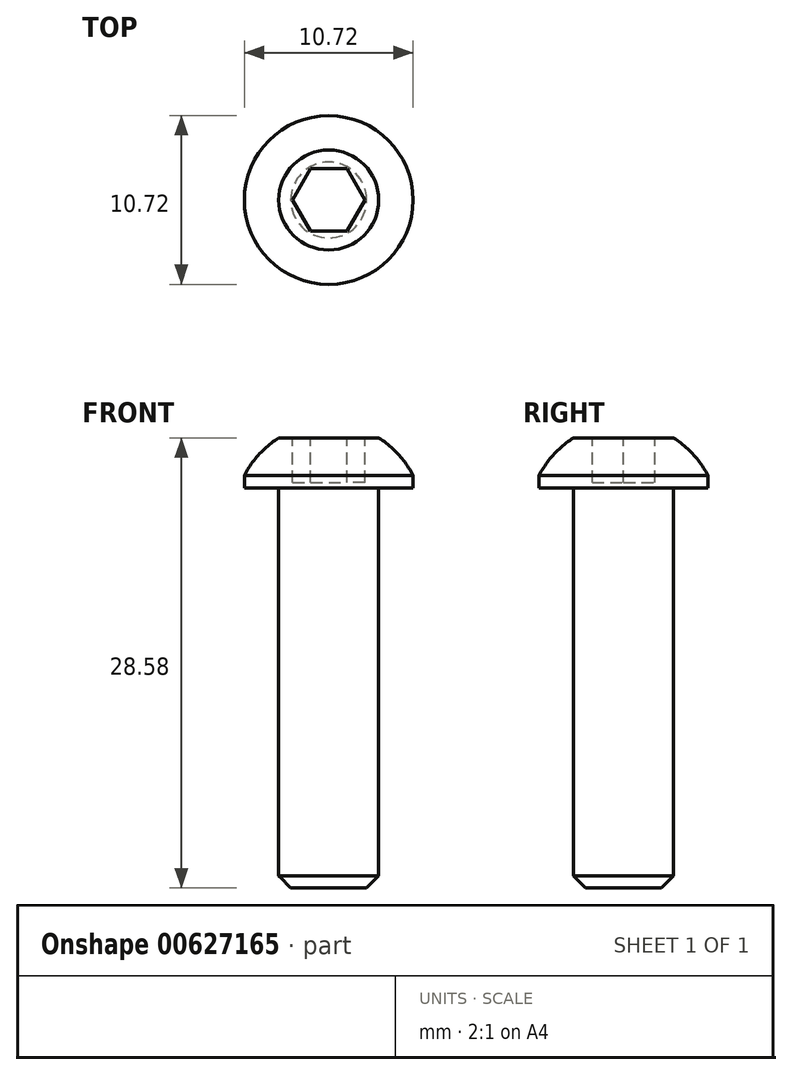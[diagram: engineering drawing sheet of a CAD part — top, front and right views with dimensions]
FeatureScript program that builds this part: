
annotation { "Feature Type Name" : "Feature", "Feature Type Description" : "" }
export const myFeature = defineFeature(function(context is Context, id is Id, definition is map)
    precondition{}
    {
        {
            var Q0;
            Q0=qCreatedBy(makeId("Front.planeOp"),FACE);
            var sketch = newSketch(context, id + "F0", { "sketchPlane" : qUnion([Q0])});
            skLineSegment(sketch, "E0", {"start": v(0, 0) * mm, "end": v(0, 25.4) * mm});
            skLineSegment(sketch, "E1", {"start": v(0, 25.4) * mm, "end": v(5.36, 25.4) * mm});
            skLineSegment(sketch, "E2", {"start": v(5.36, 25.4) * mm, "end": v(5.36, 26.19) * mm});
            skLineSegment(sketch, "E3", {"start": v(0, 25.4) * mm, "end": v(0, 28.58) * mm});
            skLineSegment(sketch, "E4", {"start": v(0, 28.58) * mm, "end": v(3.18, 28.58) * mm});
            skLineSegment(sketch, "E5.0", {"start": v(3.18, 0) * mm, "end": v(3.18, 25.4) * mm});
            skLineSegment(sketch, "E6", {"start": v(0, 0) * mm, "end": v(3.18, 0) * mm});
            skArc(sketch, "E7.trimOffspring", {"start": v(5.36, 26.19) * mm, "mid": v(4.43, 27.53) * mm, "end": v(3.18, 28.57) * mm});
            skSolve(sketch);
        }
        {
            var Q0;
            {var subQ0=sQuery(id+"F0.wireOp",EDGE,"E0");Q0=makeQuery(id+"F0.imprint","IMPRINT",FACE,{"disambiguationData":[TD([[makeQuery(id+"F0.imprint","IMPRINT",EDGE,{"derivedFrom":subQ0}),-1.0]])]});}
            var Q1;
            {var subQ1=sQuery(id+"F0.wireOp",EDGE,"E2");Q1=makeQuery(id+"F0.imprint","IMPRINT",FACE,{"disambiguationData":[TD([[makeQuery(id+"F0.imprint","IMPRINT",EDGE,{"derivedFrom":subQ1}),1.0]])]});}
            var Q2;
            Q2=sQuery(id+"F0.wireOp",EDGE,"E0");
            revolve(context, id + "F1", {"entities" : qUnion([Q0, Q1]), "axis" : qUnion([Q2]), "revolveType" : RevolveType.FULL});
        }
        {
            var Q0;
            Q0=makeQuery(id+"F1.opRevolve","SWEPT_EDGE",EDGE,{"disambiguationData":[OSD([sQuery(id+"F0.wireOp",EDGE,"E5.0"),sQuery(id+"F0.wireOp",EDGE,"E6")])]});
            chamfer(context, id + "F2", {"entities" : qUnion([Q0]), "chamferType" : ChamferType.OFFSET_ANGLE, "width" : 0.76 * mm, "oppositeDirection" : false, "angle" : 45 * degree, "tangentPropagation" : true});
        }
        {
            var Q0;
            Q0=makeQuery(id+"F1.opRevolve","SWEPT_FACE",FACE,{"disambiguationData":[OSD([sQuery(id+"F0.wireOp",EDGE,"E4")])]});
            var sketch = newSketch(context, id + "F3", { "sketchPlane" : qUnion([Q0])});
            skLineSegment(sketch, "E8.0", {"start": v(-1.15, 1.98) * mm, "end": v(1.15, 1.98) * mm});
            skLineSegment(sketch, "E8.1", {"start": v(1.15, 1.98) * mm, "end": v(2.3, 0) * mm});
            skLineSegment(sketch, "E8.2", {"start": v(2.3, 0) * mm, "end": v(1.15, -1.98) * mm});
            skLineSegment(sketch, "E8.3", {"start": v(1.15, -1.98) * mm, "end": v(-1.15, -1.98) * mm});
            skLineSegment(sketch, "E8.4", {"start": v(-1.15, -1.98) * mm, "end": v(-2.3, 0) * mm});
            skLineSegment(sketch, "E8.5", {"start": v(-2.3, 0) * mm, "end": v(-1.15, 1.98) * mm});
            skPoint(sketch, "E8.0.midPoint", {"position": v(0, 1.98) * mm});
            skSolve(sketch);
        }
        {
            var Q0;
            Q0=makeQuery(id+"F3.imprint","IMPRINT",FACE,{"disambiguationData":[TD([[makeQuery(id+"F3.imprint","IMPRINT",EDGE,{"derivedFrom":sQuery(id+"F3.wireOp",EDGE,"E8.0")}),-1.0]])]});
            extrude(context, id + "F4", {"entities" : qUnion([Q0]), "operationType" : NewBodyOperationType.REMOVE, "oppositeDirection" : true, "depth" : 2.82 * mm, "offsetDistance" : 25.4 * mm});
        }
    });
